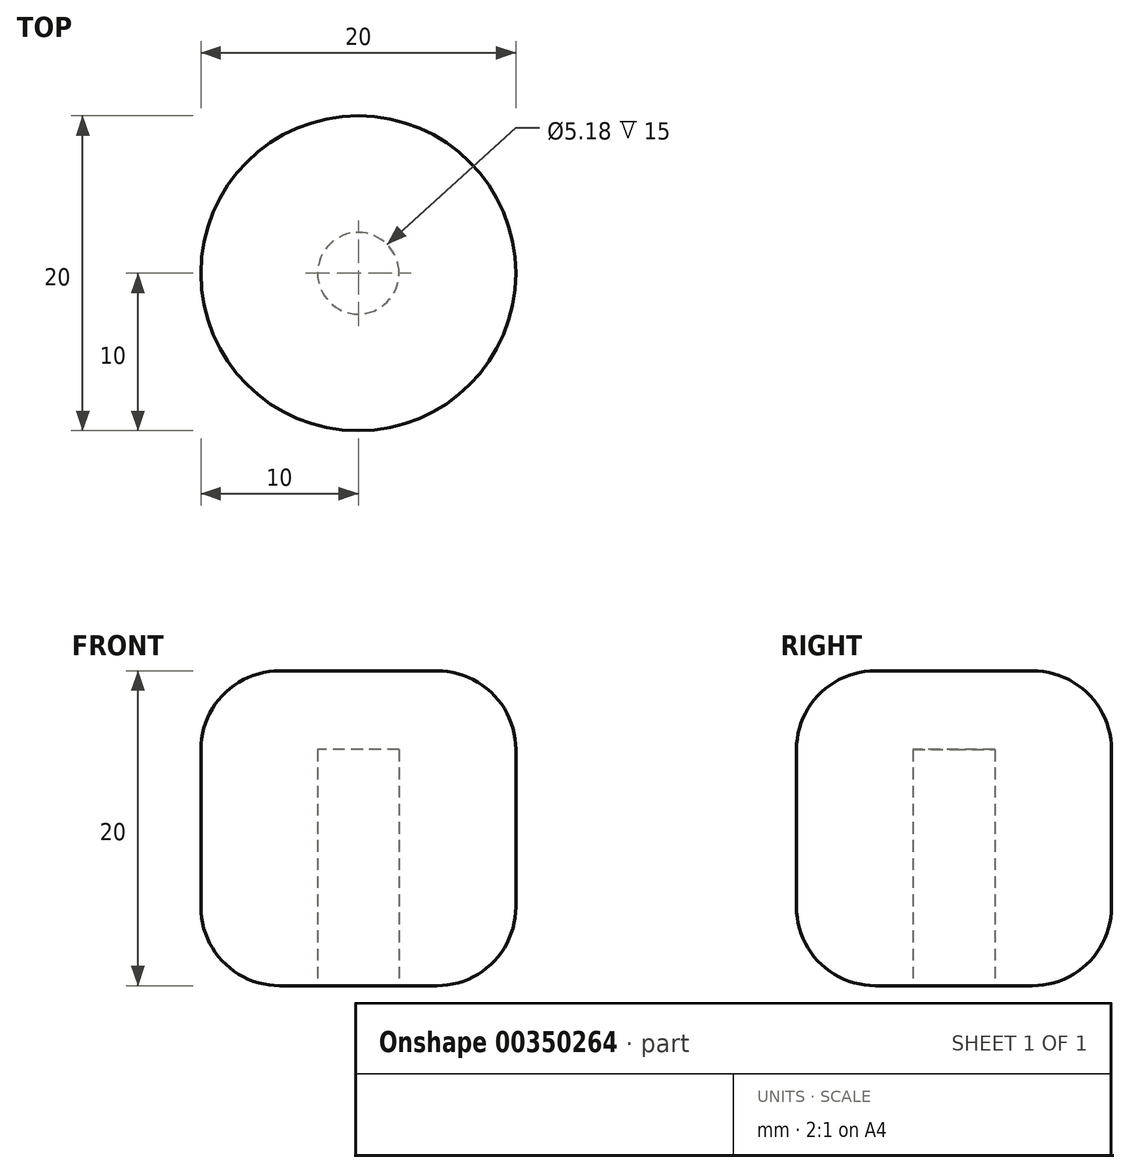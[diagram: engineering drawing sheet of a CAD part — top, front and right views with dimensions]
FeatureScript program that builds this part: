
annotation { "Feature Type Name" : "Feature", "Feature Type Description" : "" }
export const myFeature = defineFeature(function(context is Context, id is Id, definition is map)
    precondition{}
    {
        {
            var Q0;
            Q0=qCreatedBy(makeId("Top.planeOp"),FACE);
            var sketch = newSketch(context, id + "F0", { "sketchPlane" : qUnion([Q0])});
            skCircle(sketch, "E0", {"center": v(0, 0) * mm, "radius": 10 * mm});
            skSolve(sketch);
        }
        {
            var Q0;
            Q0=qCreatedBy(makeId("Top.planeOp"),FACE);
            var sketch = newSketch(context, id + "F1", { "sketchPlane" : qUnion([Q0])});
            skCircle(sketch, "E1", {"center": v(0, 0) * mm, "radius": 2.6 * mm});
            skSolve(sketch);
        }
        {
            var Q0;
            Q0 = qSketchRegion(id + "F0", true);
            extrude(context, id + "F2", {"entities" : qUnion([Q0]), "depth" : 20 * mm});
        }
        {
            var Q0;
            Q0 = qSketchRegion(id + "F1", true);
            extrude(context, id + "F3", {"entities" : qUnion([Q0]), "operationType" : NewBodyOperationType.REMOVE, "depth" : 15 * mm});
        }
        {
            var Q0;
            Q0=makeQuery(id+"F2.opExtrude","CAP_EDGE",EDGE,{"disambiguationData":[OSD([sQuery(id+"F0.wireOp",EDGE,"E0")])],"isStart":false});
            var Q1;
            Q1=makeQuery(id+"F2.opExtrude","CAP_EDGE",EDGE,{"disambiguationData":[OSD([sQuery(id+"F0.wireOp",EDGE,"E0")])],"isStart":true});
            fillet(context, id + "F4", {"entities" : qUnion([Q0, Q1]), "radius" : 5 * mm, "tangentPropagation" : true, "allowEdgeOverflow" : false});
        }
    });
